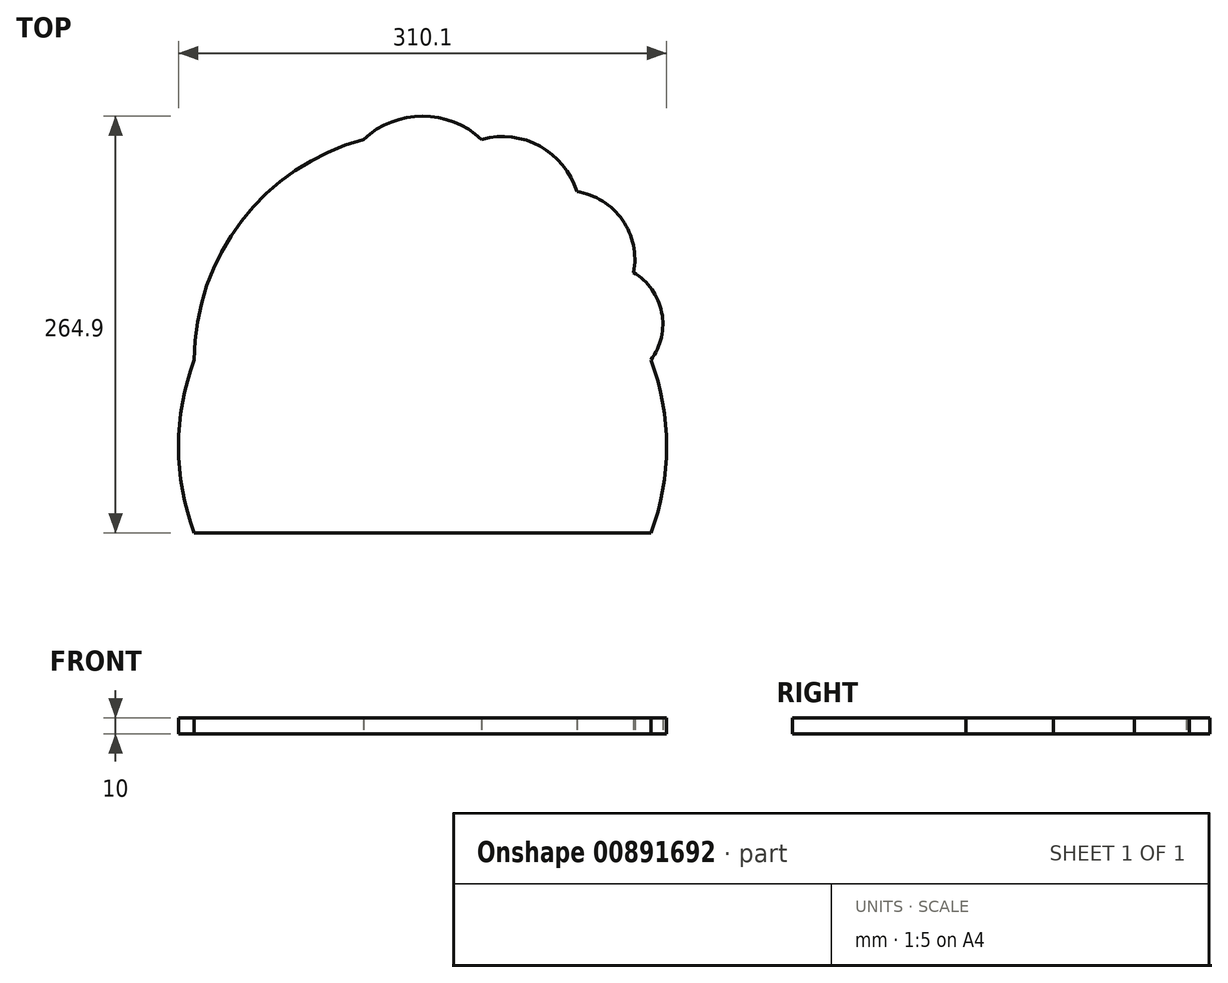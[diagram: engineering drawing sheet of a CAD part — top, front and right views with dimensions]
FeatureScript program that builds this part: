
annotation { "Feature Type Name" : "Feature", "Feature Type Description" : "" }
export const myFeature = defineFeature(function(context is Context, id is Id, definition is map)
    precondition{}
    {
        {
            var Q0;
            Q0=qCreatedBy(makeId("Top.planeOp"),FACE);
            var sketch = newSketch(context, id + "F0", { "sketchPlane" : qUnion([Q0])});
            skFitSpline(sketch, "E0.0.0", {"points": [v(222.24, 427.22) * mm, v(215.5, 429.07) * mm, v(196.44, 434.28) * mm, v(159.63, 464.69) * mm, v(135.76, 484.28) * mm]});
            skArc(sketch, "E0.0.1", {"start": v(135.76, 484.28) * mm, "mid": v(0, 567.46) * mm, "end": v(-135.76, 484.28) * mm});
            skFitSpline(sketch, "E0.0.2", {"points": [v(-135.76, 484.28) * mm, v(-159.63, 464.69) * mm, v(-196.44, 434.28) * mm, v(-215.5, 429.07) * mm, v(-222.24, 427.22) * mm]});
            skFitSpline(sketch, "E0.0.3", {"points": [v(-222.24, 427.22) * mm, v(-225.16, 426.83) * mm, v(-230.26, 426.14) * mm, v(-241.5, 428) * mm, v(-248.93, 433.28) * mm, v(-251.17, 448.34) * mm, v(-240.81, 458.85) * mm, v(-228.97, 457.5) * mm, v(-213.8, 449.01) * mm, v(-232.53, 431.49) * mm, v(-211.41, 442.33) * mm, v(-207.14, 460.38) * mm, v(-224.77, 474.32) * mm, v(-243.2, 474.95) * mm, v(-261.09, 471.32) * mm, v(-274.5, 457.58) * mm, v(-276.7, 439.28) * mm, v(-273.51, 422.75) * mm, v(-283.7, 412.03) * mm, v(-291.16, 413.34) * mm, v(-288.14, 420.98) * mm, v(-292.96, 429.6) * mm, v(-309.4, 438.45) * mm, v(-332.6, 439.06) * mm, v(-351.6, 426.46) * mm, v(-359.68, 415.35) * mm, v(-362.45, 400.5) * mm, v(-361.53, 389.94) * mm, v(-359.47, 382.27) * mm, v(-356.53, 382.37) * mm, v(-352.55, 399.36) * mm, v(-340.04, 407) * mm, v(-328.58, 408.28) * mm, v(-311.3, 404.6) * mm, v(-307.8, 389.6) * mm, v(-312.22, 380.89) * mm, v(-314.05, 379.09) * mm]});
            skArc(sketch, "E0.0.4", {"start": v(-309.42, 390.28) * mm, "mid": v(-312.68, 382.2) * mm, "end": v(-319.87, 377.3) * mm});
            skFitSpline(sketch, "E0.0.5", {"points": [v(-314.05, 379.09) * mm, v(-349.26, 368.46) * mm, v(-392.1, 351.55) * mm, v(-410.06, 337.43) * mm]});
            skEllipticalArc(sketch, "E0.0.6", {});
            skArc(sketch, "E0.0.7", {"start": v(-404.46, 196.44) * mm, "mid": v(-395.87, 191.21) * mm, "end": v(-386.4, 187.8) * mm});
            skFitSpline(sketch, "E0.0.8", {"points": [v(-394.78, 189.9) * mm, v(-344.92, 177.5) * mm, v(-241.75, 151.88) * mm, v(-181.26, 51.75) * mm, v(-150, 0) * mm]});
            skLineSegment(sketch, "E0.0.9", {"start": v(-150, 0) * mm, "end": v(-90, 0) * mm});
            skLineSegment(sketch, "E0.0.10", {"start": v(-90, 0) * mm, "end": v(-90, 110) * mm});
            skArc(sketch, "E0.0.11", {"start": v(-90, 110) * mm, "mid": v(0, 200) * mm, "end": v(90, 110) * mm});
            skLineSegment(sketch, "E0.0.12", {"start": v(90, 110) * mm, "end": v(90, 0) * mm});
            skLineSegment(sketch, "E0.0.13", {"start": v(90, 0) * mm, "end": v(150, 0) * mm});
            skFitSpline(sketch, "E0.0.14", {"points": [v(150, 0) * mm, v(181.26, 51.75) * mm, v(241.75, 151.88) * mm, v(344.92, 177.5) * mm, v(394.78, 189.9) * mm]});
            skArc(sketch, "E0.0.15", {"start": v(386.4, 187.8) * mm, "mid": v(395.87, 191.21) * mm, "end": v(404.46, 196.44) * mm});
            skEllipticalArc(sketch, "E0.0.16", {});
            skFitSpline(sketch, "E0.0.17", {"points": [v(410.06, 337.43) * mm, v(392.1, 351.55) * mm, v(349.26, 368.46) * mm, v(314.05, 379.09) * mm]});
            skArc(sketch, "E0.0.18", {"start": v(319.87, 377.3) * mm, "mid": v(312.68, 382.2) * mm, "end": v(309.42, 390.28) * mm});
            skFitSpline(sketch, "E0.0.19", {"points": [v(314.05, 379.09) * mm, v(312.22, 380.89) * mm, v(307.8, 389.6) * mm, v(311.3, 404.6) * mm, v(328.58, 408.28) * mm, v(340.04, 407) * mm, v(352.55, 399.36) * mm, v(356.53, 382.37) * mm, v(359.47, 382.27) * mm, v(361.53, 389.94) * mm, v(362.45, 400.5) * mm, v(359.68, 415.35) * mm, v(351.6, 426.46) * mm, v(332.6, 439.06) * mm, v(309.4, 438.45) * mm, v(292.96, 429.6) * mm, v(288.14, 420.98) * mm, v(291.16, 413.34) * mm, v(283.7, 412.03) * mm, v(273.51, 422.75) * mm, v(276.7, 439.28) * mm, v(274.5, 457.58) * mm, v(261.09, 471.32) * mm, v(243.2, 474.95) * mm, v(224.77, 474.32) * mm, v(207.14, 460.38) * mm, v(211.41, 442.33) * mm, v(232.53, 431.49) * mm, v(213.8, 449.01) * mm, v(228.97, 457.5) * mm, v(240.81, 458.85) * mm, v(251.17, 448.34) * mm, v(248.93, 433.28) * mm, v(241.5, 428) * mm, v(230.26, 426.14) * mm, v(225.16, 426.83) * mm, v(222.24, 427.22) * mm]});
            skLineSegment(sketch, "E1.0", {"start": v(-226.6, 290) * mm, "end": v(-165, 290) * mm});
            skLineSegment(sketch, "E1.1", {"start": v(-165, 290) * mm, "end": v(-165, 325.2) * mm});
            skLineSegment(sketch, "E1.2", {"start": v(-165, 325.2) * mm, "end": v(-226.6, 325.2) * mm});
            skLineSegment(sketch, "E1.3", {"start": v(-226.6, 290) * mm, "end": v(-226.6, 325.2) * mm});
            skLineSegment(sketch, "E1.4", {"start": v(-236.6, 290) * mm, "end": v(-236.6, 325.2) * mm});
            skLineSegment(sketch, "E1.5", {"start": v(-236.6, 325.2) * mm, "end": v(-298.2, 325.2) * mm});
            skLineSegment(sketch, "E1.6", {"start": v(-298.2, 290) * mm, "end": v(-236.6, 290) * mm});
            skLineSegment(sketch, "E1.7", {"start": v(-298.2, 290) * mm, "end": v(-298.2, 325.2) * mm});
            skLineSegment(sketch, "E2.0", {"start": v(-369.8, 290) * mm, "end": v(-308.2, 290) * mm});
            skLineSegment(sketch, "E3.0", {"start": v(-308.2, 325.2) * mm, "end": v(-369.8, 325.2) * mm});
            skLineSegment(sketch, "E4.0", {"start": v(-308.2, 290) * mm, "end": v(-308.2, 325.2) * mm});
            skLineSegment(sketch, "E5.0", {"start": v(-369.8, 290) * mm, "end": v(-369.8, 325.2) * mm});
            skFitSpline(sketch, "E6.0", {"points": [v(-342.67, 339.28) * mm, v(-317.97, 353.62) * mm, v(-277.69, 364.45) * mm, v(-252.88, 405.7) * mm, v(-252.65, 405.6) * mm, v(-252.66, 408.6) * mm]});
            skArc(sketch, "E7.0", {"start": v(-250.27, 406.87) * mm, "mid": v(-251.77, 407.17) * mm, "end": v(-252.75, 406) * mm});
            skFitSpline(sketch, "E8.0", {"points": [v(-250.27, 406.87) * mm, v(-244.43, 403.08) * mm, v(-228.6, 392.87) * mm, v(-192.33, 407.72) * mm, v(-169.18, 417.08) * mm]});
            skArc(sketch, "E9.0", {"start": v(-169.05, 414.28) * mm, "mid": v(-169.97, 415.86) * mm, "end": v(-171.8, 416.02) * mm});
            skFitSpline(sketch, "E10.0", {"points": [v(-168.95, 431.44) * mm, v(-171.46, 401.1) * mm, v(-158.84, 363.56) * mm, v(-169.18, 340.2) * mm]});
            skLineSegment(sketch, "E11.0", {"start": v(-226.24, 340.2) * mm, "end": v(-169.18, 340.2) * mm});
            skArc(sketch, "E12.0", {"start": v(-251.86, 357.45) * mm, "mid": v(-240.78, 346.25) * mm, "end": v(-226.24, 340.2) * mm});
            skArc(sketch, "E13.0", {"start": v(-252.03, 357.45) * mm, "mid": v(-263.1, 346.24) * mm, "end": v(-277.63, 340.17) * mm});
            skLineSegment(sketch, "E14.0", {"start": v(-331.71, 340.22) * mm, "end": v(-277.63, 340.17) * mm});
            skArc(sketch, "E15.0", {"start": v(-332.8, 344.66) * mm, "mid": v(-334, 342.02) * mm, "end": v(-331.71, 340.22) * mm});
            skArc(sketch, "E16.0", {"start": v(-251.86, 357.45) * mm, "mid": v(-251.95, 357.5) * mm, "end": v(-252.03, 357.45) * mm});
            skLineSegment(sketch, "E17.0", {"start": v(165, 290) * mm, "end": v(165, 325.2) * mm});
            skLineSegment(sketch, "E18.0", {"start": v(165, 290) * mm, "end": v(226.6, 290) * mm});
            skLineSegment(sketch, "E19.0", {"start": v(226.6, 290) * mm, "end": v(226.6, 325.2) * mm});
            skLineSegment(sketch, "E20.0", {"start": v(165, 325.2) * mm, "end": v(226.6, 325.2) * mm});
            skLineSegment(sketch, "E21.0", {"start": v(236.6, 325.2) * mm, "end": v(298.2, 325.2) * mm});
            skLineSegment(sketch, "E22.0", {"start": v(236.6, 290) * mm, "end": v(236.6, 325.2) * mm});
            skLineSegment(sketch, "E23.0", {"start": v(236.6, 290) * mm, "end": v(298.2, 290) * mm});
            skLineSegment(sketch, "E24.0", {"start": v(298.2, 290) * mm, "end": v(298.2, 325.2) * mm});
            skLineSegment(sketch, "E25.0", {"start": v(308.2, 290) * mm, "end": v(308.2, 325.2) * mm});
            skLineSegment(sketch, "E26.0", {"start": v(308.2, 325.2) * mm, "end": v(369.8, 325.2) * mm});
            skLineSegment(sketch, "E27.0", {"start": v(369.8, 290) * mm, "end": v(369.8, 325.2) * mm});
            skLineSegment(sketch, "E28.0", {"start": v(308.2, 290) * mm, "end": v(369.8, 290) * mm});
            skFitSpline(sketch, "E29.0", {"points": [v(342.67, 339.28) * mm, v(317.97, 353.62) * mm, v(277.69, 364.45) * mm, v(252.88, 405.7) * mm, v(252.65, 405.6) * mm, v(252.66, 408.6) * mm]});
            skArc(sketch, "E30.0", {"start": v(332.8, 344.66) * mm, "mid": v(334, 342.02) * mm, "end": v(331.71, 340.22) * mm});
            skLineSegment(sketch, "E31.0", {"start": v(331.71, 340.22) * mm, "end": v(277.63, 340.17) * mm});
            skArc(sketch, "E32.0", {"start": v(252.03, 357.45) * mm, "mid": v(263.1, 346.24) * mm, "end": v(277.63, 340.17) * mm});
            skArc(sketch, "E33.0", {"start": v(251.86, 357.45) * mm, "mid": v(240.78, 346.25) * mm, "end": v(226.24, 340.2) * mm});
            skArc(sketch, "E34.0", {"start": v(251.86, 357.45) * mm, "mid": v(251.95, 357.5) * mm, "end": v(252.03, 357.45) * mm});
            skLineSegment(sketch, "E35.0", {"start": v(226.24, 340.2) * mm, "end": v(169.18, 340.2) * mm});
            skFitSpline(sketch, "E36.0", {"points": [v(168.95, 431.44) * mm, v(171.46, 401.1) * mm, v(158.84, 363.56) * mm, v(169.18, 340.2) * mm]});
            skArc(sketch, "E37.0", {"start": v(169.05, 414.28) * mm, "mid": v(169.97, 415.86) * mm, "end": v(171.8, 416.02) * mm});
            skFitSpline(sketch, "E38.0", {"points": [v(250.27, 406.87) * mm, v(244.43, 403.08) * mm, v(228.6, 392.87) * mm, v(192.33, 407.72) * mm, v(169.18, 417.08) * mm]});
            skArc(sketch, "E39.0", {"start": v(250.27, 406.87) * mm, "mid": v(251.77, 407.17) * mm, "end": v(252.75, 406) * mm});
            skArc(sketch, "E40.0.0", {"start": v(367.9, 246.89) * mm, "mid": v(366.57, 245.65) * mm, "end": v(366.79, 243.85) * mm});
            skArc(sketch, "E40.0.1", {"start": v(366.79, 243.85) * mm, "mid": v(401.04, 245.6) * mm, "end": v(383.39, 275) * mm});
            skLineSegment(sketch, "E40.0.2", {"start": v(383.39, 275) * mm, "end": v(-383.39, 275) * mm});
            skArc(sketch, "E40.0.3", {"start": v(-383.39, 275) * mm, "mid": v(-401.04, 245.6) * mm, "end": v(-366.79, 243.85) * mm});
            skArc(sketch, "E40.0.4", {"start": v(-366.79, 243.85) * mm, "mid": v(-366.57, 245.65) * mm, "end": v(-367.9, 246.89) * mm});
            skEllipticalArc(sketch, "E40.0.5", {});
            skArc(sketch, "E40.0.6", {"start": v(-369.23, 261.25) * mm, "mid": v(-358.46, 257.25) * mm, "end": v(-353.55, 246.86) * mm});
            skArc(sketch, "E40.0.7", {"start": v(-353.55, 246.86) * mm, "mid": v(-353.08, 242.95) * mm, "end": v(-352.1, 239.13) * mm});
            skFitSpline(sketch, "E40.0.8", {"points": [v(-353.7, 243.85) * mm, v(-350.61, 235.19) * mm, v(-342.3, 200.93) * mm, v(-287.54, 161.27) * mm, v(-255.18, 135.34) * mm]});
            skFitSpline(sketch, "E40.0.9", {"points": [v(-394.78, 189.9) * mm, v(-344.92, 177.5) * mm, v(-241.75, 151.88) * mm, v(-181.26, 51.75) * mm, v(-150, 0) * mm]});
            skFitSpline(sketch, "E40.0.15", {"points": [v(150, 0) * mm, v(181.26, 51.75) * mm, v(241.75, 151.88) * mm, v(344.92, 177.5) * mm, v(394.78, 189.9) * mm]});
            skFitSpline(sketch, "E40.0.16", {"points": [v(255.18, 135.34) * mm, v(287.54, 161.27) * mm, v(342.3, 200.93) * mm, v(350.61, 235.19) * mm, v(353.7, 243.85) * mm]});
            skArc(sketch, "E40.0.17", {"start": v(352.1, 239.13) * mm, "mid": v(353.08, 242.95) * mm, "end": v(353.55, 246.86) * mm});
            skArc(sketch, "E40.0.18", {"start": v(353.55, 246.86) * mm, "mid": v(358.46, 257.25) * mm, "end": v(369.23, 261.25) * mm});
            skEllipticalArc(sketch, "E40.0.19", {});
            skLineSegment(sketch, "E41.0.0", {"start": v(305.94, 275) * mm, "end": v(-305.94, 275) * mm});
            skArc(sketch, "E41.0.1", {"start": v(-305.94, 275) * mm, "mid": v(-327.36, 237.1) * mm, "end": v(-283.84, 238.31) * mm});
            skArc(sketch, "E41.0.2", {"start": v(-283.84, 238.31) * mm, "mid": v(-283.78, 240.06) * mm, "end": v(-285.12, 241.19) * mm});
            skEllipticalArc(sketch, "E41.0.3", {});
            skFitSpline(sketch, "E41.0.4", {"points": [v(-286.27, 259.2) * mm, v(1000, -265.74) * mm, v(256.47, 1000) * mm]});
            skFitSpline(sketch, "E41.0.5", {"points": [v(-285.63, 259.1) * mm, v(1000, -265.14) * mm, v(258.09, 1000) * mm]});
            skFitSpline(sketch, "E41.0.6", {"points": [v(-265.5, 243.26) * mm, v(-263.97, 221.32) * mm, v(-260.75, 173.86) * mm, v(-230.38, 123.02) * mm, v(-214.22, 95.6) * mm]});
            skFitSpline(sketch, "E41.0.7", {"points": [v(-394.78, 189.9) * mm, v(-344.92, 177.5) * mm, v(-241.75, 151.88) * mm, v(-181.26, 51.75) * mm, v(-150, 0) * mm]});
            skFitSpline(sketch, "E41.0.13", {"points": [v(150, 0) * mm, v(181.26, 51.75) * mm, v(241.75, 151.88) * mm, v(344.92, 177.5) * mm, v(394.78, 189.9) * mm]});
            skFitSpline(sketch, "E41.0.14", {"points": [v(214.22, 95.6) * mm, v(230.38, 123.02) * mm, v(260.75, 173.86) * mm, v(263.97, 221.32) * mm, v(265.5, 243.26) * mm]});
            skFitSpline(sketch, "E41.0.15", {"points": [v(265.14, 238.31) * mm, v(1000, 265.14) * mm, v(258.09, 1000) * mm]});
            skLineSegment(sketch, "E41.0.16", {"start": v(285.63, 259.1) * mm, "end": v(286.27, 259.2) * mm});
            skEllipticalArc(sketch, "E41.0.17", {});
            skArc(sketch, "E41.0.18", {"start": v(285.12, 241.19) * mm, "mid": v(283.78, 240.06) * mm, "end": v(283.84, 238.31) * mm});
            skArc(sketch, "E41.0.19", {"start": v(283.84, 238.31) * mm, "mid": v(327.36, 237.1) * mm, "end": v(305.94, 275) * mm});
            skArc(sketch, "E42.0.0", {"start": v(188.69, 224.82) * mm, "mid": v(238.32, 232.86) * mm, "end": v(210.88, 275) * mm});
            skLineSegment(sketch, "E42.0.1", {"start": v(210.88, 275) * mm, "end": v(-210.88, 275) * mm});
            skArc(sketch, "E42.0.2", {"start": v(-210.88, 275) * mm, "mid": v(-238.32, 232.86) * mm, "end": v(-188.69, 224.82) * mm});
            skArc(sketch, "E42.0.3", {"start": v(-188.69, 224.82) * mm, "mid": v(-188.58, 226.71) * mm, "end": v(-190.1, 227.85) * mm});
            skEllipticalArc(sketch, "E42.0.4", {});
            skFitSpline(sketch, "E42.0.5", {"points": [v(-190.78, 251.9) * mm, v(1000, -168.95) * mm, v(251.9, 1000) * mm]});
            skArc(sketch, "E42.0.6", {"start": v(-170.52, 233.6) * mm, "mid": v(-170.48, 227.5) * mm, "end": v(-171.67, 221.5) * mm});
            skFitSpline(sketch, "E42.0.7", {"points": [v(-170.36, 225.76) * mm, v(-179.25, 197.05) * mm, v(-199.12, 132.86) * mm, v(-167.48, 47.3) * mm, v(-150, 0) * mm]});
            skFitSpline(sketch, "E42.0.13", {"points": [v(150, 0) * mm, v(167.48, 47.3) * mm, v(199.12, 132.86) * mm, v(179.25, 197.05) * mm, v(170.36, 225.76) * mm]});
            skArc(sketch, "E42.0.14", {"start": v(171.67, 221.5) * mm, "mid": v(170.48, 227.5) * mm, "end": v(170.52, 233.6) * mm});
            skFitSpline(sketch, "E42.0.15", {"points": [v(170.36, 225.76) * mm, v(1000, 168.95) * mm, v(251.9, 1000) * mm]});
            skEllipticalArc(sketch, "E42.0.16", {});
            skArc(sketch, "E42.0.17", {"start": v(190.1, 227.85) * mm, "mid": v(188.58, 226.71) * mm, "end": v(188.69, 224.82) * mm});
            const initialGuessF0  = {"E0.0.6": [-0.34931216680627963, 0.26310522471521947, -0.8795186508433591, 0.4758644164241295, 0.09801349999999999, 0.086147, 5.8461119226871325, 1.3987543209554119], "E0.0.16": [0.34931216680627963, 0.26310522471521947, 0.8795186508433591, 0.4758644164241295, 0.09801349999999999, 0.086147, 4.884430986224174, 0.4370733844924535], "E40.0.5": [-0.3692299729374505, 0.25402610760164496, -1, 0, 0.00868, 0.0072229875998473525, 4.71238898038469, 1.7242785659408997], "E40.0.19": [0.3692299729374472, 0.2540261076016343, 1, 0, 0.00868, 0.0072229875998473525, 4.558906741237017, 1.5707963267948966], "E41.0.3": [-0.2862692176634982, 0.25016623719894915, 1, 0, 0.01114790895395411, 0.00902888915716235, 1.5707963267948966, 4.816091749526819], "E41.0.17": [0.28626921761494883, 0.25016623719894915, 1, 0, 0.01114790895395411, 0.00902888915716235, 4.6086862112438105, 1.5707963267948968], "E42.0.4": [-0.19077662931411604, 0.2398668370838165, -1, 0, 0.012873693325351057, 0.012037203490749382, 4.71238898038469, 1.6233236227230905], "E42.0.16": [0.19077662931381673, 0.2398668370838165, -1, 0, 0.012873693325351057, 0.012037203490749382, 1.5182690308667026, 4.71238898038469]};
            skSetInitialGuess(sketch, initialGuessF0);
            skSolve(sketch);
        }
        {
            var Q0;
            Q0=qCreatedBy(makeId("Top.planeOp"),FACE);
            var sketch = newSketch(context, id + "F1", { "sketchPlane" : qUnion([Q0])});
            skLineSegment(sketch, "E43.0", {"start": v(105, 110) * mm, "end": v(105, 0) * mm});
            skArc(sketch, "E43.1", {"start": v(-105, 110) * mm, "mid": v(0, 215) * mm, "end": v(105, 110) * mm});
            skLineSegment(sketch, "E43.2", {"start": v(-105, 0) * mm, "end": v(-105, 110) * mm});
            skLineSegment(sketch, "E44.0", {"start": v(145, 110) * mm, "end": v(145, 0) * mm});
            skArc(sketch, "E44.1", {"start": v(-145, 110) * mm, "mid": v(0, 255) * mm, "end": v(145, 110) * mm});
            skLineSegment(sketch, "E44.2", {"start": v(-145, 0) * mm, "end": v(-145, 110) * mm});
            skLineSegment(sketch, "E45", {"start": v(0, 110) * mm, "end": v(0, 255) * mm, "construction": true});
            skLineSegment(sketch, "E46", {"start": v(0, 110) * mm, "end": v(145, 110) * mm, "construction": true});
            skLineSegment(sketch, "E47.0", {"start": v(125, 110) * mm, "end": v(125, 0) * mm, "construction": true});
            skArc(sketch, "E47.1", {"start": v(-125, 110) * mm, "mid": v(0, 235) * mm, "end": v(125, 110) * mm, "construction": true});
            skLineSegment(sketch, "E47.2", {"start": v(-125, 0) * mm, "end": v(-125, 110) * mm, "construction": true});
            skEllipse(sketch, "E48", {"center": v(125, 20) * mm, "majorRadius": 15 * mm, "minorRadius": 12.5 * mm, "majorAxis": v(1, 0)});
            skLineSegment(sketch, "E49.direction1", {"start": v(125, 20) * mm, "end": v(150, 20) * mm, "construction": true});
            skLineSegment(sketch, "E50", {"start": v(0, 110) * mm, "end": v(41.53, 264.97) * mm, "construction": true});
            skLineSegment(sketch, "E51", {"start": v(0, 110) * mm, "end": v(118.14, 238.93) * mm, "construction": true});
            skLineSegment(sketch, "E52", {"start": v(0, 110) * mm, "end": v(152.64, 173.22) * mm, "construction": true});
            skEllipse(sketch, "E53", {"center": v(32.35, 230.74) * mm, "majorRadius": 15 * mm, "minorRadius": 12.5 * mm, "majorAxis": v(1, 0)});
            skEllipse(sketch, "E54", {"center": v(84.45, 202.16) * mm, "majorRadius": 15 * mm, "minorRadius": 12.5 * mm, "majorAxis": v(1, 0)});
            skEllipse(sketch, "E55", {"center": v(115.48, 157.84) * mm, "majorRadius": 15 * mm, "minorRadius": 12.5 * mm, "majorAxis": v(1, 0)});
            skEllipse(sketch, "E56.0.1.0", {"center": v(125, 65) * mm, "majorRadius": 15 * mm, "minorRadius": 12.5 * mm, "majorAxis": v(1, 0)});
            skEllipse(sketch, "E56.0.2.0", {"center": v(125, 110) * mm, "majorRadius": 15 * mm, "minorRadius": 12.5 * mm, "majorAxis": v(1, 0)});
            skLineSegment(sketch, "E56.direction2", {"start": v(125, 20) * mm, "end": v(125, 65) * mm, "construction": true});
            skLineSegment(sketch, "E57.0", {"start": v(155, 110) * mm, "end": v(155, 0) * mm, "construction": true});
            skArc(sketch, "E57.1", {"start": v(-155, 110) * mm, "mid": v(0, 265) * mm, "end": v(155, 110) * mm, "construction": true});
            skLineSegment(sketch, "E57.2", {"start": v(-155, 0) * mm, "end": v(-155, 110) * mm, "construction": true});
            skArc(sketch, "E58", {"start": v(145, 0) * mm, "mid": v(155.05, 55) * mm, "end": v(145, 110) * mm});
            skArc(sketch, "E59", {"start": v(145, 110) * mm, "mid": v(151.89, 140.21) * mm, "end": v(133.96, 165.49) * mm});
            skArc(sketch, "E60", {"start": v(133.96, 165.49) * mm, "mid": v(126.95, 198.9) * mm, "end": v(97.96, 216.9) * mm});
            skArc(sketch, "E61", {"start": v(97.96, 216.9) * mm, "mid": v(74.5, 245.79) * mm, "end": v(37.53, 250.06) * mm});
            skArc(sketch, "E62", {"start": v(37.53, 250.06) * mm, "mid": v(0, 264.9) * mm, "end": v(-37.53, 250.06) * mm});
            skEllipse(sketch, "E63.MirrorC", {"center": v(-125, 20) * mm, "majorRadius": 15 * mm, "minorRadius": 12.5 * mm, "majorAxis": v(-1, 0)});
            skEllipse(sketch, "E64.MirrorC", {"center": v(-125, 65) * mm, "majorRadius": 15 * mm, "minorRadius": 12.5 * mm, "majorAxis": v(-1, 0)});
            skEllipse(sketch, "E65.MirrorC", {"center": v(-125, 110) * mm, "majorRadius": 15 * mm, "minorRadius": 12.5 * mm, "majorAxis": v(-1, 0)});
            skEllipse(sketch, "E66.MirrorC", {"center": v(-115.48, 157.84) * mm, "majorRadius": 15 * mm, "minorRadius": 12.5 * mm, "majorAxis": v(-1, 0)});
            skEllipse(sketch, "E67.MirrorC", {"center": v(-84.45, 202.16) * mm, "majorRadius": 15 * mm, "minorRadius": 12.5 * mm, "majorAxis": v(-1, 0)});
            skEllipse(sketch, "E68.MirrorC", {"center": v(-32.35, 230.74) * mm, "majorRadius": 15 * mm, "minorRadius": 12.5 * mm, "majorAxis": v(-1, 0)});
            skArc(sketch, "E69.MirrorCS", {"start": v(-97.96, 216.9) * mm, "mid": v(-74.5, 245.79) * mm, "end": v(-37.53, 250.06) * mm});
            skArc(sketch, "E70.MirrorCS", {"start": v(-133.96, 165.49) * mm, "mid": v(-126.95, 198.9) * mm, "end": v(-97.96, 216.9) * mm});
            skArc(sketch, "E71.MirrorCS", {"start": v(-145, 110) * mm, "mid": v(-151.89, 140.21) * mm, "end": v(-133.96, 165.49) * mm});
            skArc(sketch, "E72.MirrorCS", {"start": v(-145, 0) * mm, "mid": v(-155.05, 55) * mm, "end": v(-145, 110) * mm});
            skLineSegment(sketch, "E73", {"start": v(-145, 0) * mm, "end": v(-105, 0) * mm});
            skLineSegment(sketch, "E74", {"start": v(105, 0) * mm, "end": v(145, 0) * mm});
            skLineSegment(sketch, "E75.0", {"start": v(-90, 0) * mm, "end": v(-90, 110) * mm});
            skArc(sketch, "E76.0", {"start": v(-90, 110) * mm, "mid": v(0, 200) * mm, "end": v(90, 110) * mm});
            skLineSegment(sketch, "E77.0", {"start": v(90, 110) * mm, "end": v(90, 0) * mm});
            skLineSegment(sketch, "E78.0", {"start": v(90, 0) * mm, "end": v(150, 0) * mm});
            skLineSegment(sketch, "E79", {"start": v(-105, 0) * mm, "end": v(-90, 0) * mm});
            skLineSegment(sketch, "E80", {"start": v(-90, 0) * mm, "end": v(90, 0) * mm});
            skSolve(sketch);
        }
        {
            var Q0;
            {var subQ0=sQuery(id+"F1.wireOp",EDGE,"E43.0");Q0=makeQuery(id+"F1.imprint","IMPRINT",FACE,{"disambiguationData":[TD([[makeQuery(id+"F1.imprint","IMPRINT",EDGE,{"derivedFrom":subQ0}),-1.0]])]});}
            var Q1;
            {var subQ7=sQuery(id+"F1.wireOp",EDGE,"E43.0");Q1=makeQuery(id+"F1.imprint","IMPRINT",FACE,{"disambiguationData":[TD([[makeQuery(id+"F1.imprint","IMPRINT",EDGE,{"derivedFrom":subQ7}),1.0]])]});}
            var Q2;
            Q2=makeQuery(id+"F1.imprint","IMPRINT",FACE,{"disambiguationData":[TD([[makeQuery(id+"F1.imprint","IMPRINT",EDGE,{"derivedFrom":sQuery(id+"F1.wireOp",EDGE,"E44.2")}),1.0]])]});
            var Q3;
            {var subQ0=sQuery(id+"F1.wireOp",EDGE,"E71.MirrorCS");Q3=makeQuery(id+"F1.imprint","IMPRINT",FACE,{"disambiguationData":[TD([[makeQuery(id+"F1.imprint","IMPRINT",EDGE,{"derivedFrom":subQ0}),-1.0]])]});}
            var Q4;
            {var subQ0=sQuery(id+"F1.wireOp",EDGE,"E70.MirrorCS");Q4=makeQuery(id+"F1.imprint","IMPRINT",FACE,{"disambiguationData":[TD([[makeQuery(id+"F1.imprint","IMPRINT",EDGE,{"derivedFrom":subQ0}),-1.0]])]});}
            var Q5;
            {var subQ0=sQuery(id+"F1.wireOp",EDGE,"E69.MirrorCS");Q5=makeQuery(id+"F1.imprint","IMPRINT",FACE,{"disambiguationData":[TD([[makeQuery(id+"F1.imprint","IMPRINT",EDGE,{"derivedFrom":subQ0}),-1.0]])]});}
            var Q6;
            {var subQ0=sQuery(id+"F1.wireOp",EDGE,"E62");Q6=makeQuery(id+"F1.imprint","IMPRINT",FACE,{"disambiguationData":[TD([[makeQuery(id+"F1.imprint","IMPRINT",EDGE,{"derivedFrom":subQ0}),1.0]])]});}
            var Q7;
            {var subQ0=sQuery(id+"F1.wireOp",EDGE,"E61");Q7=makeQuery(id+"F1.imprint","IMPRINT",FACE,{"disambiguationData":[TD([[makeQuery(id+"F1.imprint","IMPRINT",EDGE,{"derivedFrom":subQ0}),1.0]])]});}
            var Q8;
            {var subQ0=sQuery(id+"F1.wireOp",EDGE,"E60");Q8=makeQuery(id+"F1.imprint","IMPRINT",FACE,{"disambiguationData":[TD([[makeQuery(id+"F1.imprint","IMPRINT",EDGE,{"derivedFrom":subQ0}),1.0]])]});}
            var Q9;
            {var subQ0=sQuery(id+"F1.wireOp",EDGE,"E59");Q9=makeQuery(id+"F1.imprint","IMPRINT",FACE,{"disambiguationData":[TD([[makeQuery(id+"F1.imprint","IMPRINT",EDGE,{"derivedFrom":subQ0}),1.0]])]});}
            var Q10;
            Q10=makeQuery(id+"F1.imprint","IMPRINT",FACE,{"disambiguationData":[TD([[makeQuery(id+"F1.imprint","IMPRINT",EDGE,{"derivedFrom":sQuery(id+"F1.wireOp",EDGE,"E44.0")}),1.0]])]});
            var Q11;
            Q11=makeQuery(id+"F1.imprint","IMPRINT",FACE,{"disambiguationData":[TD([[makeQuery(id+"F1.imprint","IMPRINT",EDGE,{"derivedFrom":sQuery(id+"F1.wireOp",EDGE,"E48")}),1.0]])]});
            var Q12;
            Q12=makeQuery(id+"F1.imprint","IMPRINT",FACE,{"disambiguationData":[TD([[makeQuery(id+"F1.imprint","IMPRINT",EDGE,{"derivedFrom":sQuery(id+"F1.wireOp",EDGE,"E56.0.1.0")}),1.0]])]});
            var Q13;
            Q13=makeQuery(id+"F1.imprint","IMPRINT",FACE,{"disambiguationData":[TD([[makeQuery(id+"F1.imprint","IMPRINT",EDGE,{"derivedFrom":sQuery(id+"F1.wireOp",EDGE,"E56.0.2.0")}),1.0]])]});
            var Q14;
            Q14=makeQuery(id+"F1.imprint","IMPRINT",FACE,{"disambiguationData":[TD([[makeQuery(id+"F1.imprint","IMPRINT",EDGE,{"derivedFrom":sQuery(id+"F1.wireOp",EDGE,"E55")}),1.0]])]});
            var Q15;
            Q15=makeQuery(id+"F1.imprint","IMPRINT",FACE,{"disambiguationData":[TD([[makeQuery(id+"F1.imprint","IMPRINT",EDGE,{"derivedFrom":sQuery(id+"F1.wireOp",EDGE,"E54")}),1.0]])]});
            var Q16;
            Q16=makeQuery(id+"F1.imprint","IMPRINT",FACE,{"disambiguationData":[TD([[makeQuery(id+"F1.imprint","IMPRINT",EDGE,{"derivedFrom":sQuery(id+"F1.wireOp",EDGE,"E53")}),1.0]])]});
            var Q17;
            Q17=makeQuery(id+"F1.imprint","IMPRINT",FACE,{"disambiguationData":[TD([[makeQuery(id+"F1.imprint","IMPRINT",EDGE,{"derivedFrom":sQuery(id+"F1.wireOp",EDGE,"E68.MirrorC")}),1.0]])]});
            var Q18;
            Q18=makeQuery(id+"F1.imprint","IMPRINT",FACE,{"disambiguationData":[TD([[makeQuery(id+"F1.imprint","IMPRINT",EDGE,{"derivedFrom":sQuery(id+"F1.wireOp",EDGE,"E67.MirrorC")}),1.0]])]});
            var Q19;
            Q19=makeQuery(id+"F1.imprint","IMPRINT",FACE,{"disambiguationData":[TD([[makeQuery(id+"F1.imprint","IMPRINT",EDGE,{"derivedFrom":sQuery(id+"F1.wireOp",EDGE,"E66.MirrorC")}),1.0]])]});
            var Q20;
            Q20=makeQuery(id+"F1.imprint","IMPRINT",FACE,{"disambiguationData":[TD([[makeQuery(id+"F1.imprint","IMPRINT",EDGE,{"derivedFrom":sQuery(id+"F1.wireOp",EDGE,"E65.MirrorC")}),1.0]])]});
            var Q21;
            Q21=makeQuery(id+"F1.imprint","IMPRINT",FACE,{"disambiguationData":[TD([[makeQuery(id+"F1.imprint","IMPRINT",EDGE,{"derivedFrom":sQuery(id+"F1.wireOp",EDGE,"E64.MirrorC")}),1.0]])]});
            var Q22;
            Q22=makeQuery(id+"F1.imprint","IMPRINT",FACE,{"disambiguationData":[TD([[makeQuery(id+"F1.imprint","IMPRINT",EDGE,{"derivedFrom":sQuery(id+"F1.wireOp",EDGE,"E63.MirrorC")}),1.0]])]});
            var Q23;
            Q23=makeQuery(id+"F1.imprint","IMPRINT",FACE,{"disambiguationData":[TD([[makeQuery(id+"F1.imprint","IMPRINT",EDGE,{"derivedFrom":sQuery(id+"F1.wireOp",EDGE,"E75.0")}),-1.0]])]});
            extrude(context, id + "F2", {"entities" : qUnion([Q0, Q1, Q2, Q3, Q4, Q5, Q6, Q7, Q8, Q9, Q10, Q11, Q12, Q13, Q14, Q15, Q16, Q17, Q18, Q19, Q20, Q21, Q22, Q23]), "depth" : 10 * mm, "offsetDistance" : 25 * mm});
        }
        {
            var Q0;
            Q0=makeQuery(id+"F2.opExtrude","CAP_FACE",FACE,{"disambiguationData":[OSD([sQuery(id+"F1.wireOp",EDGE,"E58"),sQuery(id+"F1.wireOp",EDGE,"E59"),sQuery(id+"F1.wireOp",EDGE,"E60"),sQuery(id+"F1.wireOp",EDGE,"E61"),sQuery(id+"F1.wireOp",EDGE,"E62"),sQuery(id+"F1.wireOp",EDGE,"E69.MirrorCS"),sQuery(id+"F1.wireOp",EDGE,"E70.MirrorCS"),sQuery(id+"F1.wireOp",EDGE,"E71.MirrorCS"),sQuery(id+"F1.wireOp",EDGE,"E72.MirrorCS"),sQuery(id+"F1.wireOp",EDGE,"E73"),sQuery(id+"F1.wireOp",EDGE,"E78.0"),sQuery(id+"F1.wireOp",EDGE,"E79"),sQuery(id+"F1.wireOp",EDGE,"E80")])],"isStart":false});
            cPlane(context, id + "F3", {"entities" : qUnion([Q0]), "cplaneType" : CPlaneType.OFFSET, "offset" : 50 * mm, "width" : 150 * mm, "height" : 150 * mm});
        }
    });
